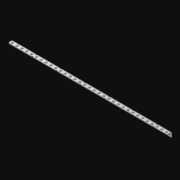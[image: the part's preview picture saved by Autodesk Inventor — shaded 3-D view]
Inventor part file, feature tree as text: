
AUTODESK INVENTOR PART (.ipt)
format: ipt  version: 2021 (Build 250183000, 183)  size: 859,136 bytes
history: native  units: in
note: dims shown in document units (in); Inventor stores cm internally (conversion verified against a paired STEP export)
features: extrude x67, other x66, sketch x3, pattern_linear x1, sheet_metal_op x1
ambient origin geometry x8: Origin, YZ Plane, XZ Plane, XY Plane, X Axis, Y Axis, Z Axis, Center Point
bodies: Solid1 (feature_tree)
feature tree (138):
  pattern_linear  "Rectangular Pattern1"  Spacing1=0.063in  [1 undecoded]
  extrude  "Extrusion1"  Depth=0.5in
  sketch  "Sketch1"  dims[d0=0.182in]
  other  "Srf1"
  sketch  "Sketch2"  dims[d1=0.063in d2=0.0in]
  other  "Srf2"
  other  "Srf3"
  other  "Srf5"
  other  "Srf7"
  other  "Srf9"
  other  "Srf11"
  other  "Srf13"
  other  "Srf15"
  other  "Srf17"
  other  "Srf19"
  other  "Srf21"
  other  "Srf23"
  other  "Srf25"
  other  "Srf27"
  other  "Srf29"
  other  "Srf31"
  other  "Srf33"
  other  "Srf35"
  other  "Srf37"
  other  "Srf39"
  other  "Srf41"
  other  "Srf43"
  other  "Srf45"
  other  "Srf47"
  other  "Srf49"
  other  "Srf51"
  other  "Srf53"
  other  "Srf55"
  other  "Srf57"
  other  "Srf59"
  other  "Srf61"
  other  "Srf63"
  other  "Srf65"
  other  "Srf4"
  other  "Srf6"
  other  "Srf8"
  other  "Srf10"
  other  "Srf12"
  other  "Srf14"
  other  "Srf16"
  other  "Srf18"
  other  "Srf20"
  other  "Srf22"
  other  "Srf24"
  other  "Srf26"
  other  "Srf28"
  other  "Srf30"
  other  "Srf32"
  other  "Srf34"
  other  "Srf36"
  other  "Srf38"
  other  "Srf40"
  other  "Srf42"
  other  "Srf44"
  other  "Srf46"
  other  "Srf48"
  other  "Srf50"
  other  "Srf52"
  other  "Srf54"
  other  "Srf56"
  other  "Srf58"
  other  "Srf60"
  other  "Srf62"
  other  "Srf64"
  other  "Srf66"
  sketch  "Sketch3"  dims[d3=0.182in d4=0.063in d5=0.0in d8=0.5in d9=1.0in d10=0.0in]
  sheet_metal_op  "Fold1"
  extrude  "ExtrusionSrf1"  Depth=1.0in TaperAngle=0.0deg
  extrude  "ExtrusionSrf2"  [1 undecoded]
  extrude  "ExtrusionSrf3"  [1 undecoded]
  extrude  "ExtrusionSrf4"  [1 undecoded]
  extrude  "ExtrusionSrf5"  [1 undecoded]
  extrude  "ExtrusionSrf6"  [1 undecoded]
  extrude  "ExtrusionSrf7"  [1 undecoded]
  extrude  "ExtrusionSrf8"  [1 undecoded]
  extrude  "ExtrusionSrf9"  [1 undecoded]
  extrude  "ExtrusionSrf10"  [1 undecoded]
  extrude  "ExtrusionSrf11"  [1 undecoded]
  extrude  "ExtrusionSrf12"  [1 undecoded]
  extrude  "ExtrusionSrf13"  [1 undecoded]
  extrude  "ExtrusionSrf14"  [1 undecoded]
  extrude  "ExtrusionSrf15"  [1 undecoded]
  extrude  "ExtrusionSrf16"  [1 undecoded]
  extrude  "ExtrusionSrf17"  [1 undecoded]
  extrude  "ExtrusionSrf18"  [1 undecoded]
  extrude  "ExtrusionSrf19"  [1 undecoded]
  extrude  "ExtrusionSrf20"  [1 undecoded]
  extrude  "ExtrusionSrf21"  [1 undecoded]
  extrude  "ExtrusionSrf22"  [1 undecoded]
  extrude  "ExtrusionSrf23"  [1 undecoded]
  extrude  "ExtrusionSrf24"  [1 undecoded]
  extrude  "ExtrusionSrf25"  [1 undecoded]
  extrude  "ExtrusionSrf26"  [1 undecoded]
  extrude  "ExtrusionSrf27"  [1 undecoded]
  extrude  "ExtrusionSrf28"  [1 undecoded]
  extrude  "ExtrusionSrf29"  [1 undecoded]
  extrude  "ExtrusionSrf30"  [1 undecoded]
  extrude  "ExtrusionSrf31"  [1 undecoded]
  extrude  "ExtrusionSrf32"  [1 undecoded]
  extrude  "ExtrusionSrf33"  [1 undecoded]
  extrude  "ExtrusionSrf34"  [1 undecoded]
  extrude  "ExtrusionSrf37"  [1 undecoded]
  extrude  "ExtrusionSrf38"  [1 undecoded]
  extrude  "ExtrusionSrf39"  [1 undecoded]
  extrude  "ExtrusionSrf40"  [1 undecoded]
  extrude  "ExtrusionSrf41"  [1 undecoded]
  extrude  "ExtrusionSrf42"  [1 undecoded]
  extrude  "ExtrusionSrf43"  [1 undecoded]
  extrude  "ExtrusionSrf44"  [1 undecoded]
  extrude  "ExtrusionSrf45"  [1 undecoded]
  extrude  "ExtrusionSrf46"  [1 undecoded]
  extrude  "ExtrusionSrf47"  [1 undecoded]
  extrude  "ExtrusionSrf48"  [1 undecoded]
  extrude  "ExtrusionSrf49"  [1 undecoded]
  extrude  "ExtrusionSrf50"  [1 undecoded]
  extrude  "ExtrusionSrf51"  [1 undecoded]
  extrude  "ExtrusionSrf52"  [1 undecoded]
  extrude  "ExtrusionSrf53"  [1 undecoded]
  extrude  "ExtrusionSrf54"  [1 undecoded]
  extrude  "ExtrusionSrf55"  [1 undecoded]
  extrude  "ExtrusionSrf56"  [1 undecoded]
  extrude  "ExtrusionSrf57"  [1 undecoded]
  extrude  "ExtrusionSrf58"  [1 undecoded]
  extrude  "ExtrusionSrf59"  [1 undecoded]
  extrude  "ExtrusionSrf60"  [1 undecoded]
  extrude  "ExtrusionSrf61"  [1 undecoded]
  extrude  "ExtrusionSrf62"  [1 undecoded]
  extrude  "ExtrusionSrf63"  [1 undecoded]
  extrude  "ExtrusionSrf64"  [1 undecoded]
  extrude  "ExtrusionSrf65"  [1 undecoded]
  extrude  "ExtrusionSrf66"  [1 undecoded]
  extrude  "ExtrusionSrf67"  [1 undecoded]
  extrude  "ExtrusionSrf68"  [1 undecoded]
note: 66 required parameter values undecoded (feature->parameter linkage not recoverable at this tier; creation-order binding heuristic only, values carry confidence <= 0.55)
